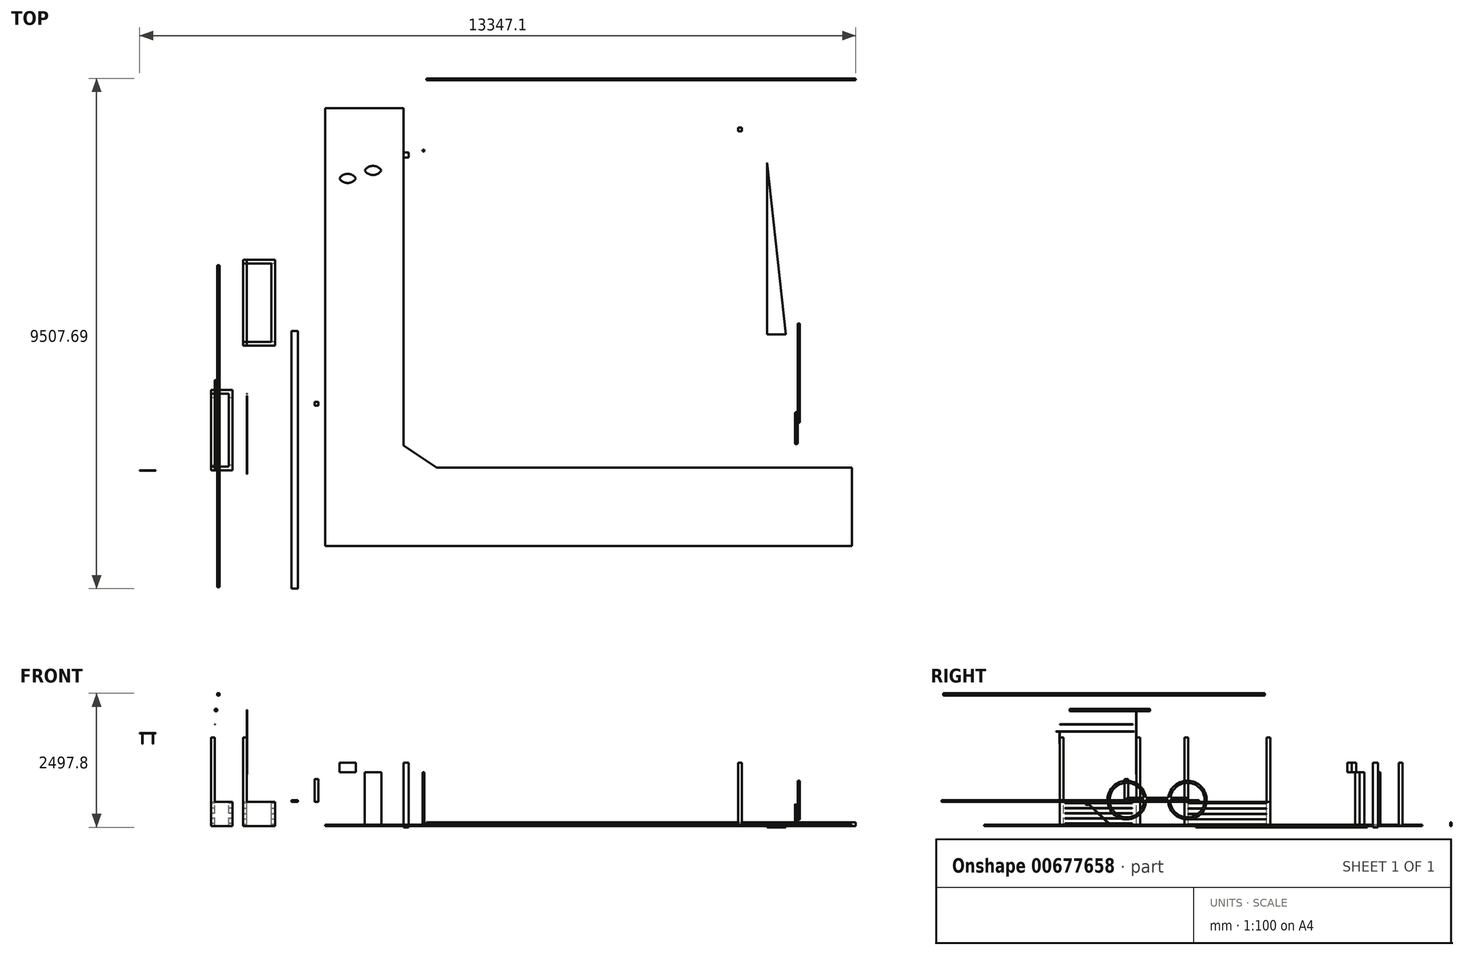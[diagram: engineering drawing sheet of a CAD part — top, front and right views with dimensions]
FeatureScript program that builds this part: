
annotation { "Feature Type Name" : "Feature", "Feature Type Description" : "" }
export const myFeature = defineFeature(function(context is Context, id is Id, definition is map)
    precondition{}
    {
        {
            var Q0;
            Q0=qCreatedBy(makeId("Top.planeOp"),FACE);
            var sketch = newSketch(context, id + "F0", { "sketchPlane" : qUnion([Q0])});
            skLineSegment(sketch, "E0.bottom", {"start": v(-6724.28, 5845.8) * mm, "end": v(50.72, 5845.8) * mm});
            skLineSegment(sketch, "E0.top", {"start": v(-6103.03, 165.8) * mm, "end": v(50.72, 165.8) * mm});
            skLineSegment(sketch, "E0.left", {"start": v(-6724.28, 5845.8) * mm, "end": v(-6724.28, 575.92) * mm});
            skLineSegment(sketch, "E0.right", {"start": v(50.72, 5845.8) * mm, "end": v(50.72, 165.8) * mm});
            skLineSegment(sketch, "E1.bottom", {"start": v(-449.28, 5845.8) * mm, "end": v(-379.28, 5845.8) * mm});
            skLineSegment(sketch, "E1.top", {"start": v(-449.28, 5915.8) * mm, "end": v(-379.28, 5915.8) * mm});
            skLineSegment(sketch, "E1.left", {"start": v(-449.28, 5845.8) * mm, "end": v(-449.28, 5915.8) * mm});
            skLineSegment(sketch, "E1.right", {"start": v(-379.28, 5845.8) * mm, "end": v(-379.28, 5915.8) * mm});
            skLineSegment(sketch, "E2.bottom", {"start": v(-2184.28, 5845.8) * mm, "end": v(-2254.28, 5845.8) * mm});
            skLineSegment(sketch, "E2.top", {"start": v(-2184.28, 5915.8) * mm, "end": v(-2254.28, 5915.8) * mm});
            skLineSegment(sketch, "E2.left", {"start": v(-2184.28, 5845.8) * mm, "end": v(-2184.28, 5915.8) * mm});
            skLineSegment(sketch, "E2.right", {"start": v(-2254.28, 5845.8) * mm, "end": v(-2254.28, 5915.8) * mm});
            skLineSegment(sketch, "E3.bottom", {"start": v(-4054.28, 5845.8) * mm, "end": v(-3984.28, 5845.8) * mm});
            skLineSegment(sketch, "E3.top", {"start": v(-4054.28, 5915.8) * mm, "end": v(-3984.28, 5915.8) * mm});
            skLineSegment(sketch, "E3.left", {"start": v(-4054.28, 5845.8) * mm, "end": v(-4054.28, 5915.8) * mm});
            skLineSegment(sketch, "E3.right", {"start": v(-3984.28, 5845.8) * mm, "end": v(-3984.28, 5915.8) * mm});
            skLineSegment(sketch, "E4.bottom", {"start": v(-5869.28, 5845.8) * mm, "end": v(-5799.28, 5845.8) * mm});
            skLineSegment(sketch, "E4.top", {"start": v(-5869.28, 5915.8) * mm, "end": v(-5799.28, 5915.8) * mm});
            skLineSegment(sketch, "E4.left", {"start": v(-5869.28, 5845.8) * mm, "end": v(-5869.28, 5915.8) * mm});
            skLineSegment(sketch, "E4.right", {"start": v(-5799.28, 5845.8) * mm, "end": v(-5799.28, 5915.8) * mm});
            skLineSegment(sketch, "E5.bottom", {"start": v(-6724.28, 5945.8) * mm, "end": v(-6629.28, 5945.8) * mm});
            skLineSegment(sketch, "E5.top", {"start": v(-6724.28, 6040.8) * mm, "end": v(-6629.28, 6040.8) * mm});
            skLineSegment(sketch, "E5.left", {"start": v(-6724.28, 5945.8) * mm, "end": v(-6724.28, 6040.8) * mm});
            skLineSegment(sketch, "E5.right", {"start": v(-6629.28, 5945.8) * mm, "end": v(-6629.28, 6040.8) * mm});
            skLineSegment(sketch, "E6", {"start": v(-6724.28, 575.92) * mm, "end": v(-6314.16, 165.8) * mm});
            skLineSegment(sketch, "E7", {"start": v(50.72, 5845.8) * mm, "end": v(50.72, 2645.8) * mm});
            skLineSegment(sketch, "E8", {"start": v(50.72, 2645.8) * mm, "end": v(400.72, 2645.8) * mm});
            skLineSegment(sketch, "E9", {"start": v(400.72, 2645.8) * mm, "end": v(50.72, 5845.8) * mm});
            skLineSegment(sketch, "E10", {"start": v(400.72, 2645.8) * mm, "end": v(671.97, 165.8) * mm});
            skLineSegment(sketch, "E11", {"start": v(50.72, 165.8) * mm, "end": v(671.97, 165.8) * mm});
            skLineSegment(sketch, "E12", {"start": v(-6724.28, 5845.8) * mm, "end": v(-6103.03, 165.8) * mm});
            skSolve(sketch);
        }
        {
            var Q0;
            Q0=makeQuery(id+"F0.imprint","IMPRINT",FACE,{"disambiguationData":[TD([[makeQuery(id+"F0.imprint","IMPRINT",EDGE,{"derivedFrom":sQuery(id+"F0.wireOp",EDGE,"E0.top")}),1.0]])]});
            var Q1;
            Q1=makeQuery(id+"F0.imprint","IMPRINT",FACE,{"disambiguationData":[TD([[makeQuery(id+"F0.imprint","IMPRINT",EDGE,{"derivedFrom":sQuery(id+"F0.wireOp",EDGE,"E1.bottom")}),1.0]])]});
            var Q2;
            Q2=makeQuery(id+"F0.imprint","IMPRINT",FACE,{"disambiguationData":[TD([[makeQuery(id+"F0.imprint","IMPRINT",EDGE,{"derivedFrom":sQuery(id+"F0.wireOp",EDGE,"E2.bottom")}),-1.0]])]});
            var Q3;
            Q3=makeQuery(id+"F0.imprint","IMPRINT",FACE,{"disambiguationData":[TD([[makeQuery(id+"F0.imprint","IMPRINT",EDGE,{"derivedFrom":sQuery(id+"F0.wireOp",EDGE,"E3.bottom")}),1.0]])]});
            var Q4;
            Q4=makeQuery(id+"F0.imprint","IMPRINT",FACE,{"disambiguationData":[TD([[makeQuery(id+"F0.imprint","IMPRINT",EDGE,{"derivedFrom":sQuery(id+"F0.wireOp",EDGE,"E4.bottom")}),1.0]])]});
            var Q5;
            Q5=makeQuery(id+"F0.imprint","IMPRINT",FACE,{"disambiguationData":[TD([[makeQuery(id+"F0.imprint","IMPRINT",EDGE,{"derivedFrom":sQuery(id+"F0.wireOp",EDGE,"E5.bottom")}),1.0]])]});
            var Q6;
            Q6=makeQuery(id+"F0.imprint","IMPRINT",FACE,{"disambiguationData":[TD([[makeQuery(id+"F0.imprint","IMPRINT",EDGE,{"derivedFrom":sQuery(id+"F0.wireOp",EDGE,"E0.right")}),1.0]])]});
            var Q7;
            Q7=makeQuery(id+"F0.imprint","IMPRINT",FACE,{"disambiguationData":[TD([[makeQuery(id+"F0.imprint","IMPRINT",EDGE,{"derivedFrom":sQuery(id+"F0.wireOp",EDGE,"E7")}),1.0]])]});
            extrude(context, id + "F1", {"entities" : qUnion([Q0, Q1, Q2, Q3, Q4, Q5, Q6, Q7]), "oppositeDirection" : true, "depth" : 25 * mm, "offsetDistance" : 25 * mm});
        }
        {
            var Q0;
            Q0=qCreatedBy(makeId("Top.planeOp"),FACE);
            var sketch = newSketch(context, id + "F2", { "sketchPlane" : qUnion([Q0])});
            skLineSegment(sketch, "E13.bottom", {"start": v(-484.06, 6502.45) * mm, "end": v(-414.06, 6502.45) * mm});
            skLineSegment(sketch, "E13.top", {"start": v(-484.06, 6432.45) * mm, "end": v(-414.06, 6432.45) * mm});
            skLineSegment(sketch, "E13.left", {"start": v(-484.06, 6502.45) * mm, "end": v(-484.06, 6432.45) * mm});
            skLineSegment(sketch, "E13.right", {"start": v(-414.06, 6502.45) * mm, "end": v(-414.06, 6432.45) * mm});
            skSolve(sketch);
        }
        {
            var Q0;
            Q0=makeQuery(id+"F2.imprint","IMPRINT",FACE,{"disambiguationData":[TD([[makeQuery(id+"F2.imprint","IMPRINT",EDGE,{"derivedFrom":sQuery(id+"F2.wireOp",EDGE,"E13.bottom")}),-1.0]])]});
            extrude(context, id + "F3", {"entities" : qUnion([Q0]), "depth" : 1180 * mm, "offsetDistance" : 25 * mm});
        }
        {
            var Q0;
            Q0=makeQuery(id+"F1.opExtrude","CAP_FACE",FACE,{"disambiguationData":[OSD([sQuery(id+"F0.wireOp",EDGE,"E5.bottom"),sQuery(id+"F0.wireOp",EDGE,"E5.top"),sQuery(id+"F0.wireOp",EDGE,"E5.left"),sQuery(id+"F0.wireOp",EDGE,"E5.right")])],"isStart":true});
            extrude(context, id + "F4", {"entities" : qUnion([Q0]), "operationType" : NewBodyOperationType.ADD, "depth" : 1180 * mm, "offsetDistance" : 25 * mm});
        }
        {
            var Q0;
            Q0=qCreatedBy(makeId("Top.planeOp"),FACE);
            var sketch = newSketch(context, id + "F5", { "sketchPlane" : qUnion([Q0])});
            skLineSegment(sketch, "E14.bottom", {"start": v(-6295.07, 7386.85) * mm, "end": v(1704.93, 7386.85) * mm});
            skLineSegment(sketch, "E14.top", {"start": v(-6295.07, 7416.85) * mm, "end": v(1704.93, 7416.85) * mm});
            skLineSegment(sketch, "E14.left", {"start": v(-6295.07, 7386.85) * mm, "end": v(-6295.07, 7416.85) * mm});
            skLineSegment(sketch, "E14.right", {"start": v(1704.93, 7386.85) * mm, "end": v(1704.93, 7416.85) * mm});
            skSolve(sketch);
        }
        {
            var Q0;
            Q0=makeQuery(id+"F5.imprint","IMPRINT",FACE,{"disambiguationData":[TD([[makeQuery(id+"F5.imprint","IMPRINT",EDGE,{"derivedFrom":sQuery(id+"F5.wireOp",EDGE,"E14.bottom")}),1.0]])]});
            extrude(context, id + "F6", {"entities" : qUnion([Q0]), "depth" : 70 * mm, "offsetDistance" : 25 * mm});
        }
        {
            var Q0;
            Q0=qCreatedBy(makeId("Top.planeOp"),FACE);
            var sketch = newSketch(context, id + "F7", { "sketchPlane" : qUnion([Q0])});
            skArc(sketch, "E15", {"start": v(-7135.8, 5703.5) * mm, "mid": v(-7290.8, 5788.5) * mm, "end": v(-7445.8, 5703.5) * mm});
            skLineSegment(sketch, "E16", {"start": v(-7477.04, 5788.5) * mm, "end": v(-7088.43, 5788.5) * mm});
            skLineSegment(sketch, "E17", {"start": v(-7445.8, 5703.5) * mm, "end": v(-7135.8, 5703.5) * mm});
            skArc(sketch, "E18.MirrorCS", {"start": v(-7135.8, 5703.5) * mm, "mid": v(-7290.8, 5618.5) * mm, "end": v(-7445.8, 5703.5) * mm});
            skSolve(sketch);
        }
        {
            var Q0;
            {var subQ1=sQuery(id+"F7.wireOp",EDGE,"E17");Q0=makeQuery(id+"F7.imprint","IMPRINT",FACE,{"disambiguationData":[TD([[makeQuery(id+"F7.imprint","IMPRINT",EDGE,{"derivedFrom":subQ1}),1.0]])]});}
            var Q1;
            Q1=makeQuery(id+"F7.imprint","IMPRINT",FACE,{"disambiguationData":[TD([[makeQuery(id+"F7.imprint","IMPRINT",EDGE,{"derivedFrom":sQuery(id+"F7.wireOp",EDGE,"E17")}),-1.0]])]});
            extrude(context, id + "F8", {"entities" : qUnion([Q0, Q1]), "depth" : 1000 * mm, "offsetDistance" : 25 * mm});
        }
        {
            var Q0;
            Q0=qCreatedBy(makeId("Top.planeOp"),FACE);
            var sketch = newSketch(context, id + "F9", { "sketchPlane" : qUnion([Q0])});
            skLineSegment(sketch, "E19.bottom", {"start": v(-6366.97, 6054.53) * mm, "end": v(-6331.97, 6054.53) * mm});
            skLineSegment(sketch, "E19.top", {"start": v(-6366.97, 6089.53) * mm, "end": v(-6331.97, 6089.53) * mm});
            skLineSegment(sketch, "E19.left", {"start": v(-6366.97, 6054.53) * mm, "end": v(-6366.97, 6089.53) * mm});
            skLineSegment(sketch, "E19.right", {"start": v(-6331.97, 6054.53) * mm, "end": v(-6331.97, 6089.53) * mm});
            skSolve(sketch);
        }
        {
            var Q0;
            Q0=makeQuery(id+"F9.imprint","IMPRINT",FACE,{"disambiguationData":[TD([[makeQuery(id+"F9.imprint","IMPRINT",EDGE,{"derivedFrom":sQuery(id+"F9.wireOp",EDGE,"E19.bottom")}),1.0]])]});
            extrude(context, id + "F10", {"entities" : qUnion([Q0]), "depth" : 1000 * mm, "offsetDistance" : 25 * mm});
        }
        {
            var Q0;
            Q0=qCreatedBy(makeId("Top.planeOp"),FACE);
            var sketch = newSketch(context, id + "F11", { "sketchPlane" : qUnion([Q0])});
            skLineSegment(sketch, "E20.bottom", {"start": v(-9714.32, 4035.91) * mm, "end": v(-9114.32, 4035.91) * mm});
            skLineSegment(sketch, "E20.top", {"start": v(-9714.32, 2435.91) * mm, "end": v(-9114.32, 2435.91) * mm});
            skLineSegment(sketch, "E20.left", {"start": v(-9714.32, 4035.91) * mm, "end": v(-9714.32, 2435.91) * mm});
            skLineSegment(sketch, "E20.right", {"start": v(-9114.32, 4035.91) * mm, "end": v(-9114.32, 2435.91) * mm});
            skSolve(sketch);
        }
        {
            var Q0;
            Q0=makeQuery(id+"F11.imprint","IMPRINT",FACE,{"disambiguationData":[TD([[makeQuery(id+"F11.imprint","IMPRINT",EDGE,{"derivedFrom":sQuery(id+"F11.wireOp",EDGE,"E20.bottom")}),-1.0]])]});
            extrude(context, id + "F12", {"entities" : qUnion([Q0]), "depth" : 450 * mm, "offsetDistance" : 25 * mm});
        }
        {
            var Q0;
            Q0=makeQuery(id+"F12.opExtrude","SWEPT_FACE",FACE,{"disambiguationData":[OSD([sQuery(id+"F11.wireOp",EDGE,"E20.left")])]});
            var sketch = newSketch(context, id + "F13", { "sketchPlane" : qUnion([Q0])});
            skLineSegment(sketch, "E21.bottom", {"start": v(-3965.91, 428) * mm, "end": v(-2505.91, 428) * mm});
            skLineSegment(sketch, "E21.top", {"start": v(-3965.91, 423) * mm, "end": v(-2505.91, 423) * mm});
            skLineSegment(sketch, "E21.left", {"start": v(-3965.91, 428) * mm, "end": v(-3965.91, 423) * mm});
            skLineSegment(sketch, "E21.right", {"start": v(-2505.91, 428) * mm, "end": v(-2505.91, 423) * mm});
            skLineSegment(sketch, "E22.0.1.0", {"start": v(-3965.91, 328) * mm, "end": v(-2505.91, 328) * mm});
            skLineSegment(sketch, "E22.0.1.1", {"start": v(-3965.91, 323) * mm, "end": v(-2505.91, 323) * mm});
            skLineSegment(sketch, "E22.0.1.2", {"start": v(-3965.91, 328) * mm, "end": v(-3965.91, 323) * mm});
            skLineSegment(sketch, "E22.0.1.3", {"start": v(-2505.91, 328) * mm, "end": v(-2505.91, 323) * mm});
            skLineSegment(sketch, "E22.0.2.0", {"start": v(-3965.91, 228) * mm, "end": v(-2505.91, 228) * mm});
            skLineSegment(sketch, "E22.0.2.1", {"start": v(-3965.91, 223) * mm, "end": v(-2505.91, 223) * mm});
            skLineSegment(sketch, "E22.0.2.2", {"start": v(-3965.91, 228) * mm, "end": v(-3965.91, 223) * mm});
            skLineSegment(sketch, "E22.0.2.3", {"start": v(-2505.91, 228) * mm, "end": v(-2505.91, 223) * mm});
            skLineSegment(sketch, "E22.0.3.0", {"start": v(-3965.91, 128) * mm, "end": v(-2505.91, 128) * mm});
            skLineSegment(sketch, "E22.0.3.1", {"start": v(-3965.91, 123) * mm, "end": v(-2505.91, 123) * mm});
            skLineSegment(sketch, "E22.0.3.2", {"start": v(-3965.91, 128) * mm, "end": v(-3965.91, 123) * mm});
            skLineSegment(sketch, "E22.0.3.3", {"start": v(-2505.91, 128) * mm, "end": v(-2505.91, 123) * mm});
            skLineSegment(sketch, "E22.0.4.0", {"start": v(-3965.91, 28) * mm, "end": v(-2505.91, 28) * mm});
            skLineSegment(sketch, "E22.0.4.1", {"start": v(-3965.91, 23) * mm, "end": v(-2505.91, 23) * mm});
            skLineSegment(sketch, "E22.0.4.2", {"start": v(-3965.91, 28) * mm, "end": v(-3965.91, 23) * mm});
            skLineSegment(sketch, "E22.0.4.3", {"start": v(-2505.91, 28) * mm, "end": v(-2505.91, 23) * mm});
            skLineSegment(sketch, "E22.0.5.0", {"start": v(-3965.91, -72) * mm, "end": v(-2505.91, -72) * mm});
            skLineSegment(sketch, "E22.0.5.1", {"start": v(-3965.91, -77) * mm, "end": v(-2505.91, -77) * mm});
            skLineSegment(sketch, "E22.0.5.2", {"start": v(-3965.91, -72) * mm, "end": v(-3965.91, -77) * mm});
            skLineSegment(sketch, "E22.0.5.3", {"start": v(-2505.91, -72) * mm, "end": v(-2505.91, -77) * mm});
            skLineSegment(sketch, "E22.0.6.0", {"start": v(-3965.91, -172) * mm, "end": v(-2505.91, -172) * mm});
            skLineSegment(sketch, "E22.0.6.1", {"start": v(-3965.91, -177) * mm, "end": v(-2505.91, -177) * mm});
            skLineSegment(sketch, "E22.0.6.2", {"start": v(-3965.91, -172) * mm, "end": v(-3965.91, -177) * mm});
            skLineSegment(sketch, "E22.0.6.3", {"start": v(-2505.91, -172) * mm, "end": v(-2505.91, -177) * mm});
            skLineSegment(sketch, "E22.0.7.0", {"start": v(-3965.91, -272) * mm, "end": v(-2505.91, -272) * mm});
            skLineSegment(sketch, "E22.0.7.1", {"start": v(-3965.91, -277) * mm, "end": v(-2505.91, -277) * mm});
            skLineSegment(sketch, "E22.0.7.2", {"start": v(-3965.91, -272) * mm, "end": v(-3965.91, -277) * mm});
            skLineSegment(sketch, "E22.0.7.3", {"start": v(-2505.91, -272) * mm, "end": v(-2505.91, -277) * mm});
            skLineSegment(sketch, "E22.0.8.0", {"start": v(-3965.91, -372) * mm, "end": v(-2505.91, -372) * mm});
            skLineSegment(sketch, "E22.0.8.1", {"start": v(-3965.91, -377) * mm, "end": v(-2505.91, -377) * mm});
            skLineSegment(sketch, "E22.0.8.2", {"start": v(-3965.91, -372) * mm, "end": v(-3965.91, -377) * mm});
            skLineSegment(sketch, "E22.0.8.3", {"start": v(-2505.91, -372) * mm, "end": v(-2505.91, -377) * mm});
            skLineSegment(sketch, "E22.direction1", {"start": v(-3965.91, 423) * mm, "end": v(-3652.23, 423) * mm, "construction": true});
            skLineSegment(sketch, "E22.direction2", {"start": v(-3965.91, 423) * mm, "end": v(-3965.91, 323) * mm, "construction": true});
            skSolve(sketch);
        }
        {
            var Q0;
            Q0=makeQuery(id+"F13.imprint","IMPRINT",FACE,{"disambiguationData":[TD([[makeQuery(id+"F13.imprint","IMPRINT",EDGE,{"derivedFrom":sQuery(id+"F13.wireOp",EDGE,"E21.bottom")}),-1.0]])]});
            var Q1;
            Q1=makeQuery(id+"F13.imprint","IMPRINT",FACE,{"disambiguationData":[TD([[makeQuery(id+"F13.imprint","IMPRINT",EDGE,{"derivedFrom":sQuery(id+"F13.wireOp",EDGE,"E22.0.1.0")}),-1.0]])]});
            var Q2;
            Q2=makeQuery(id+"F13.imprint","IMPRINT",FACE,{"disambiguationData":[TD([[makeQuery(id+"F13.imprint","IMPRINT",EDGE,{"derivedFrom":sQuery(id+"F13.wireOp",EDGE,"E22.0.2.0")}),-1.0]])]});
            var Q3;
            Q3=makeQuery(id+"F13.imprint","IMPRINT",FACE,{"disambiguationData":[TD([[makeQuery(id+"F13.imprint","IMPRINT",EDGE,{"derivedFrom":sQuery(id+"F13.wireOp",EDGE,"E22.0.3.0")}),-1.0]])]});
            var Q4;
            Q4=makeQuery(id+"F13.imprint","IMPRINT",FACE,{"disambiguationData":[TD([[makeQuery(id+"F13.imprint","IMPRINT",EDGE,{"derivedFrom":sQuery(id+"F13.wireOp",EDGE,"E22.0.4.0")}),-1.0]])]});
            var Q5;
            Q5=makeQuery(id+"F13.imprint","IMPRINT",FACE,{"disambiguationData":[TD([[makeQuery(id+"F13.imprint","IMPRINT",EDGE,{"derivedFrom":sQuery(id+"F13.wireOp",EDGE,"E22.0.5.0")}),-1.0]])]});
            var Q6;
            Q6=makeQuery(id+"F13.imprint","IMPRINT",FACE,{"disambiguationData":[TD([[makeQuery(id+"F13.imprint","IMPRINT",EDGE,{"derivedFrom":sQuery(id+"F13.wireOp",EDGE,"E22.0.6.0")}),-1.0]])]});
            var Q7;
            Q7=makeQuery(id+"F13.imprint","IMPRINT",FACE,{"disambiguationData":[TD([[makeQuery(id+"F13.imprint","IMPRINT",EDGE,{"derivedFrom":sQuery(id+"F13.wireOp",EDGE,"E22.0.7.0")}),-1.0]])]});
            var Q8;
            Q8=makeQuery(id+"F13.imprint","IMPRINT",FACE,{"disambiguationData":[TD([[makeQuery(id+"F13.imprint","IMPRINT",EDGE,{"derivedFrom":sQuery(id+"F13.wireOp",EDGE,"E22.0.8.0")}),-1.0]])]});
            extrude(context, id + "F14", {"entities" : qUnion([Q0, Q1, Q2, Q3, Q4, Q5, Q6, Q7, Q8]), "operationType" : NewBodyOperationType.REMOVE, "oppositeDirection" : true, "depth" : 700 * mm, "offsetDistance" : 25 * mm});
        }
        {
            var Q0;
            Q0=makeQuery(id+"F12.opExtrude","CAP_FACE",FACE,{"disambiguationData":[OSD([sQuery(id+"F11.wireOp",EDGE,"E20.bottom"),sQuery(id+"F11.wireOp",EDGE,"E20.top"),sQuery(id+"F11.wireOp",EDGE,"E20.left"),sQuery(id+"F11.wireOp",EDGE,"E20.right")])],"isStart":false});
            var sketch = newSketch(context, id + "F15", { "sketchPlane" : qUnion([Q0])});
            skLineSegment(sketch, "E23.bottom", {"start": v(-9714.32, 4035.91) * mm, "end": v(-9644.32, 4035.91) * mm});
            skLineSegment(sketch, "E23.top", {"start": v(-9714.32, 3965.91) * mm, "end": v(-9644.32, 3965.91) * mm});
            skLineSegment(sketch, "E23.left", {"start": v(-9714.32, 4035.91) * mm, "end": v(-9714.32, 3965.91) * mm});
            skLineSegment(sketch, "E23.right", {"start": v(-9644.32, 4035.91) * mm, "end": v(-9644.32, 3965.91) * mm});
            skLineSegment(sketch, "E24.bottom", {"start": v(-9714.32, 2435.91) * mm, "end": v(-9644.32, 2435.91) * mm});
            skLineSegment(sketch, "E24.top", {"start": v(-9714.32, 2505.91) * mm, "end": v(-9644.32, 2505.91) * mm});
            skLineSegment(sketch, "E24.left", {"start": v(-9714.32, 2435.91) * mm, "end": v(-9714.32, 2505.91) * mm});
            skLineSegment(sketch, "E24.right", {"start": v(-9644.32, 2435.91) * mm, "end": v(-9644.32, 2505.91) * mm});
            skSolve(sketch);
        }
        {
            var Q0;
            Q0=makeQuery(id+"F15.imprint","IMPRINT",FACE,{"disambiguationData":[TD([[makeQuery(id+"F15.imprint","IMPRINT",EDGE,{"derivedFrom":sQuery(id+"F15.wireOp",EDGE,"E23.bottom")}),-1.0]])]});
            var Q1;
            Q1=makeQuery(id+"F15.imprint","IMPRINT",FACE,{"disambiguationData":[TD([[makeQuery(id+"F15.imprint","IMPRINT",EDGE,{"derivedFrom":sQuery(id+"F15.wireOp",EDGE,"E24.bottom")}),1.0]])]});
            extrude(context, id + "F16", {"entities" : qUnion([Q0, Q1]), "operationType" : NewBodyOperationType.ADD, "depth" : 1200 * mm, "offsetDistance" : 25 * mm});
        }
        {
            var Q0;
            Q0=makeQuery(id+"F16.opExtrude","SWEPT_FACE",FACE,{"disambiguationData":[OSD([sQuery(id+"F15.wireOp",EDGE,"E24.right")])]});
            var sketch = newSketch(context, id + "F17", { "sketchPlane" : qUnion([Q0])});
            skLineSegment(sketch, "E25.bottom", {"start": v(43.28, 1763.08) * mm, "end": v(1503.28, 1763.08) * mm});
            skLineSegment(sketch, "E25.top", {"start": v(43.28, 1758.08) * mm, "end": v(1503.28, 1758.08) * mm});
            skLineSegment(sketch, "E25.left", {"start": v(43.28, 1763.08) * mm, "end": v(43.28, 1758.08) * mm});
            skLineSegment(sketch, "E25.right", {"start": v(1503.28, 1763.08) * mm, "end": v(1503.28, 1758.08) * mm});
            skLineSegment(sketch, "E26.bottom", {"start": v(1534.4, 2162.34) * mm, "end": v(1539.4, 2162.34) * mm});
            skLineSegment(sketch, "E26.top", {"start": v(1534.4, 962.34) * mm, "end": v(1539.4, 962.34) * mm});
            skLineSegment(sketch, "E26.left", {"start": v(1534.4, 2162.34) * mm, "end": v(1534.4, 962.34) * mm});
            skLineSegment(sketch, "E26.right", {"start": v(1539.4, 2162.34) * mm, "end": v(1539.4, 962.34) * mm});
            skSolve(sketch);
        }
        {
            var Q0;
            Q0=makeQuery(id+"F17.imprint","IMPRINT",FACE,{"disambiguationData":[TD([[makeQuery(id+"F17.imprint","IMPRINT",EDGE,{"derivedFrom":sQuery(id+"F17.wireOp",EDGE,"E25.bottom")}),-1.0]])]});
            var Q1;
            Q1=makeQuery(id+"F17.imprint","IMPRINT",FACE,{"disambiguationData":[TD([[makeQuery(id+"F17.imprint","IMPRINT",EDGE,{"derivedFrom":sQuery(id+"F17.wireOp",EDGE,"E26.bottom")}),-1.0]])]});
            extrude(context, id + "F18", {"entities" : qUnion([Q0, Q1]), "depth" : 5 * mm, "offsetDistance" : 25 * mm});
        }
        {
            var Q0;
            Q0=makeQuery(id+"F12.opExtrude","CAP_FACE",FACE,{"disambiguationData":[OSD([sQuery(id+"F11.wireOp",EDGE,"E20.bottom"),sQuery(id+"F11.wireOp",EDGE,"E20.top"),sQuery(id+"F11.wireOp",EDGE,"E20.left"),sQuery(id+"F11.wireOp",EDGE,"E20.right")])],"isStart":false});
            var sketch = newSketch(context, id + "F19", { "sketchPlane" : qUnion([Q0])});
            skLineSegment(sketch, "E27.bottom", {"start": v(-9644.32, 3965.91) * mm, "end": v(-9184.32, 3965.91) * mm});
            skLineSegment(sketch, "E27.top", {"start": v(-9644.32, 2505.91) * mm, "end": v(-9184.32, 2505.91) * mm});
            skLineSegment(sketch, "E27.left", {"start": v(-9644.32, 3965.91) * mm, "end": v(-9644.32, 2505.91) * mm});
            skLineSegment(sketch, "E27.right", {"start": v(-9184.32, 3965.91) * mm, "end": v(-9184.32, 2505.91) * mm});
            skSolve(sketch);
        }
        {
            var Q0;
            Q0=makeQuery(id+"F19.imprint","IMPRINT",FACE,{"disambiguationData":[TD([[makeQuery(id+"F19.imprint","IMPRINT",EDGE,{"derivedFrom":sQuery(id+"F19.wireOp",EDGE,"E27.bottom")}),-1.0]])]});
            extrude(context, id + "F20", {"entities" : qUnion([Q0]), "operationType" : NewBodyOperationType.REMOVE, "oppositeDirection" : true, "depth" : 680 * mm, "offsetDistance" : 25 * mm});
        }
        {
            var Q0;
            Q0=makeQuery(id+"F8.opExtrude","CAP_FACE",FACE,{"disambiguationData":[OSD([sQuery(id+"F7.wireOp",EDGE,"E15"),sQuery(id+"F7.wireOp",EDGE,"E18.MirrorCS")])],"isStart":false});
            var sketch = newSketch(context, id + "F21", { "sketchPlane" : qUnion([Q0])});
            skLineSegment(sketch, "E28", {"start": v(-7918.47, 5554) * mm, "end": v(-7608.47, 5554) * mm});
            skLineSegment(sketch, "E29", {"start": v(-7608.47, 5554) * mm, "end": v(-7608.47, 5639) * mm});
            skLineSegment(sketch, "E30", {"start": v(-7608.47, 5639) * mm, "end": v(-8001.82, 5639) * mm});
            skArc(sketch, "E31", {"start": v(-7608.47, 5554) * mm, "mid": v(-7763.47, 5639) * mm, "end": v(-7918.47, 5554) * mm});
            skArc(sketch, "E32.MirrorCS", {"start": v(-7608.47, 5554) * mm, "mid": v(-7763.47, 5469) * mm, "end": v(-7918.47, 5554) * mm});
            skSolve(sketch);
        }
        {
            var Q0;
            {var subQ0=sQuery(id+"F21.wireOp",EDGE,"E28");Q0=makeQuery(id+"F21.imprint","IMPRINT",FACE,{"disambiguationData":[TD([[makeQuery(id+"F21.imprint","IMPRINT",EDGE,{"derivedFrom":subQ0}),1.0]])]});}
            var Q1;
            Q1=makeQuery(id+"F21.imprint","IMPRINT",FACE,{"disambiguationData":[TD([[makeQuery(id+"F21.imprint","IMPRINT",EDGE,{"derivedFrom":sQuery(id+"F21.wireOp",EDGE,"E28")}),-1.0]])]});
            extrude(context, id + "F22", {"entities" : qUnion([Q0, Q1]), "depth" : 180 * mm, "offsetDistance" : 25 * mm});
        }
        {
            var Q0;
            Q0=makeQuery(id+"F1.opExtrude","CAP_FACE",FACE,{"disambiguationData":[OSD([sQuery(id+"F0.wireOp",EDGE,"E0.bottom"),sQuery(id+"F0.wireOp",EDGE,"E0.top"),sQuery(id+"F0.wireOp",EDGE,"E0.left"),sQuery(id+"F0.wireOp",EDGE,"E0.right"),sQuery(id+"F0.wireOp",EDGE,"E1.top"),sQuery(id+"F0.wireOp",EDGE,"E1.left"),sQuery(id+"F0.wireOp",EDGE,"E1.right"),sQuery(id+"F0.wireOp",EDGE,"E2.top"),sQuery(id+"F0.wireOp",EDGE,"E2.left"),sQuery(id+"F0.wireOp",EDGE,"E2.right"),sQuery(id+"F0.wireOp",EDGE,"E3.top"),sQuery(id+"F0.wireOp",EDGE,"E3.left"),sQuery(id+"F0.wireOp",EDGE,"E3.right"),sQuery(id+"F0.wireOp",EDGE,"E4.top"),sQuery(id+"F0.wireOp",EDGE,"E4.left"),sQuery(id+"F0.wireOp",EDGE,"E4.right"),sQuery(id+"F0.wireOp",EDGE,"E6")])],"isStart":true});
            var sketch = newSketch(context, id + "F23", { "sketchPlane" : qUnion([Q0])});
            skLineSegment(sketch, "E33", {"start": v(-6724.28, 5845.8) * mm, "end": v(-6724.28, 575.92) * mm});
            skLineSegment(sketch, "E34", {"start": v(-6724.28, 575.92) * mm, "end": v(-6103.03, 165.8) * mm});
            skLineSegment(sketch, "E35", {"start": v(-6103.03, 165.8) * mm, "end": v(1636.76, 165.8) * mm});
            skLineSegment(sketch, "E36", {"start": v(1636.76, 165.8) * mm, "end": v(1636.76, -1294.2) * mm});
            skLineSegment(sketch, "E37", {"start": v(1636.76, -1294.2) * mm, "end": v(-8184.28, -1294.2) * mm});
            skLineSegment(sketch, "E38", {"start": v(-8184.28, -1294.2) * mm, "end": v(-8184.28, 6866.58) * mm});
            skLineSegment(sketch, "E39", {"start": v(-8184.28, 6866.58) * mm, "end": v(-6724.28, 6866.58) * mm});
            skLineSegment(sketch, "E40", {"start": v(-6724.28, 6866.58) * mm, "end": v(-6724.28, 5845.8) * mm});
            skSolve(sketch);
        }
        {
            var Q0;
            Q0=makeQuery(id+"F23.imprint","IMPRINT",FACE,{"disambiguationData":[TD([[makeQuery(id+"F23.imprint","IMPRINT",EDGE,{"derivedFrom":sQuery(id+"F23.wireOp",EDGE,"E33")}),-1.0]])]});
            extrude(context, id + "F24", {"entities" : qUnion([Q0]), "depth" : 25 * mm, "offsetDistance" : 25 * mm});
        }
        {
            var Q0;
            Q0=makeQuery(id+"F1.opExtrude","CAP_FACE",FACE,{"disambiguationData":[OSD([sQuery(id+"F0.wireOp",EDGE,"E0.bottom"),sQuery(id+"F0.wireOp",EDGE,"E0.top"),sQuery(id+"F0.wireOp",EDGE,"E0.left"),sQuery(id+"F0.wireOp",EDGE,"E0.right"),sQuery(id+"F0.wireOp",EDGE,"E1.top"),sQuery(id+"F0.wireOp",EDGE,"E1.left"),sQuery(id+"F0.wireOp",EDGE,"E1.right"),sQuery(id+"F0.wireOp",EDGE,"E2.top"),sQuery(id+"F0.wireOp",EDGE,"E2.left"),sQuery(id+"F0.wireOp",EDGE,"E2.right"),sQuery(id+"F0.wireOp",EDGE,"E3.top"),sQuery(id+"F0.wireOp",EDGE,"E3.left"),sQuery(id+"F0.wireOp",EDGE,"E3.right"),sQuery(id+"F0.wireOp",EDGE,"E4.top"),sQuery(id+"F0.wireOp",EDGE,"E4.left"),sQuery(id+"F0.wireOp",EDGE,"E4.right"),sQuery(id+"F0.wireOp",EDGE,"E6")])],"isStart":true});
            var sketch = newSketch(context, id + "F25", { "sketchPlane" : qUnion([Q0])});
            skLineSegment(sketch, "E41.bottom", {"start": v(599.92, 1199.52) * mm, "end": v(597.92, 1199.52) * mm});
            skLineSegment(sketch, "E41.top", {"start": v(599.92, 599.52) * mm, "end": v(597.92, 599.52) * mm});
            skLineSegment(sketch, "E41.left", {"start": v(623.92, 1175.52) * mm, "end": v(623.92, 623.52) * mm});
            skLineSegment(sketch, "E41.right", {"start": v(573.92, 1175.52) * mm, "end": v(573.92, 623.52) * mm});
            skPoint(sketch, "E42.visualSharp", {"position": v(573.92, 1199.52) * mm});
            skArc(sketch, "E42.filletArc", {"start": v(597.92, 1199.52) * mm, "mid": v(580.95, 1192.5) * mm, "end": v(573.92, 1175.52) * mm});
            skPoint(sketch, "E43.visualSharp", {"position": v(623.92, 1199.52) * mm});
            skArc(sketch, "E43.filletArc", {"start": v(623.92, 1175.52) * mm, "mid": v(616.9, 1192.5) * mm, "end": v(599.92, 1199.52) * mm});
            skPoint(sketch, "E44.visualSharp", {"position": v(623.92, 599.52) * mm});
            skArc(sketch, "E44.filletArc", {"start": v(599.92, 599.52) * mm, "mid": v(616.9, 606.55) * mm, "end": v(623.92, 623.52) * mm});
            skPoint(sketch, "E45.visualSharp", {"position": v(573.92, 599.52) * mm});
            skArc(sketch, "E45.filletArc", {"start": v(573.92, 623.52) * mm, "mid": v(580.95, 606.55) * mm, "end": v(597.92, 599.52) * mm});
            skArc(sketch, "E46.0", {"start": v(597.92, 1191.52) * mm, "mid": v(586.6, 1186.84) * mm, "end": v(581.92, 1175.52) * mm});
            skLineSegment(sketch, "E46.1", {"start": v(599.92, 1191.52) * mm, "end": v(597.92, 1191.52) * mm});
            skLineSegment(sketch, "E46.2", {"start": v(581.92, 1175.52) * mm, "end": v(581.92, 623.52) * mm});
            skArc(sketch, "E46.3", {"start": v(615.92, 1175.52) * mm, "mid": v(611.23, 1186.84) * mm, "end": v(599.92, 1191.52) * mm});
            skArc(sketch, "E46.4", {"start": v(581.92, 623.52) * mm, "mid": v(586.6, 612.21) * mm, "end": v(597.92, 607.52) * mm});
            skLineSegment(sketch, "E46.5", {"start": v(599.92, 607.52) * mm, "end": v(597.92, 607.52) * mm});
            skArc(sketch, "E46.6", {"start": v(599.92, 607.52) * mm, "mid": v(611.23, 612.21) * mm, "end": v(615.92, 623.52) * mm});
            skLineSegment(sketch, "E46.7", {"start": v(615.92, 1175.52) * mm, "end": v(615.92, 623.52) * mm});
            skSolve(sketch);
        }
        {
            var Q0;
            Q0=makeQuery(id+"F25.imprint","IMPRINT",FACE,{"disambiguationData":[TD([[makeQuery(id+"F25.imprint","IMPRINT",EDGE,{"derivedFrom":sQuery(id+"F25.wireOp",EDGE,"E41.bottom")}),1.0]])]});
            extrude(context, id + "F26", {"entities" : qUnion([Q0]), "depth" : 400 * mm, "offsetDistance" : 25 * mm});
        }
        {
            var Q0;
            Q0=makeQuery(id+"F26.opExtrude","SWEPT_FACE",FACE,{"disambiguationData":[OSD([sQuery(id+"F25.wireOp",EDGE,"E41.left")])]});
            var sketch = newSketch(context, id + "F27", { "sketchPlane" : qUnion([Q0])});
            skLineSegment(sketch, "E47", {"start": v(400.9, 392) * mm, "end": v(664.2, 392) * mm});
            skLineSegment(sketch, "E48", {"start": v(664.2, 392) * mm, "end": v(1065.78, 0) * mm});
            skLineSegment(sketch, "E49", {"start": v(1065.78, 0) * mm, "end": v(1075.44, 0) * mm});
            skLineSegment(sketch, "E50", {"start": v(1075.44, 0) * mm, "end": v(1075.44, -239.66) * mm});
            skLineSegment(sketch, "E51", {"start": v(1075.44, -239.66) * mm, "end": v(417.05, -229.8) * mm});
            skLineSegment(sketch, "E52", {"start": v(417.05, -229.8) * mm, "end": v(400.9, 392) * mm});
            skLineSegment(sketch, "E53", {"start": v(667.45, 400) * mm, "end": v(1069.04, 8) * mm});
            skLineSegment(sketch, "E54", {"start": v(1069.04, 8) * mm, "end": v(1266.16, 8) * mm});
            skLineSegment(sketch, "E55", {"start": v(1266.16, 8) * mm, "end": v(1215.61, 445.54) * mm});
            skLineSegment(sketch, "E56", {"start": v(1215.61, 445.54) * mm, "end": v(670.1, 465.26) * mm});
            skLineSegment(sketch, "E57", {"start": v(670.1, 465.26) * mm, "end": v(667.45, 400) * mm});
            skSolve(sketch);
        }
        {
            var Q0;
            {var subQ0=sQuery(id+"F27.wireOp",EDGE,"E49");Q0=makeQuery(id+"F27.imprint","IMPRINT",FACE,{"disambiguationData":[TD([[makeQuery(id+"F27.imprint","IMPRINT",EDGE,{"derivedFrom":subQ0}),1.0]])]});}
            var Q1;
            {var subQ0=sQuery(id+"F27.wireOp",EDGE,"E48");Q1=makeQuery(id+"F27.imprint","IMPRINT",FACE,{"disambiguationData":[TD([[makeQuery(id+"F27.imprint","IMPRINT",EDGE,{"derivedFrom":subQ0}),-1.0]])]});}
            var Q2;
            {var subQ1=sQuery(id+"F27.wireOp",EDGE,"E55");Q2=makeQuery(id+"F27.imprint","IMPRINT",FACE,{"disambiguationData":[TD([[makeQuery(id+"F27.imprint","IMPRINT",EDGE,{"derivedFrom":subQ1}),1.0]])]});}
            var Q3;
            {var subQ0=sQuery(id+"F27.wireOp",EDGE,"E53");Q3=makeQuery(id+"F27.imprint","IMPRINT",FACE,{"disambiguationData":[TD([[makeQuery(id+"F27.imprint","IMPRINT",EDGE,{"derivedFrom":subQ0}),1.0]])]});}
            extrude(context, id + "F28", {"entities" : qUnion([Q0, Q1, Q2, Q3]), "operationType" : NewBodyOperationType.REMOVE, "oppositeDirection" : true, "depth" : 55 * mm, "offsetDistance" : 25 * mm});
        }
        {
            var Q0;
            Q0=makeQuery(id+"F26.opExtrude","SWEPT_FACE",FACE,{"disambiguationData":[OSD([sQuery(id+"F25.wireOp",EDGE,"E41.left")])]});
            var sketch = newSketch(context, id + "F29", { "sketchPlane" : qUnion([Q0])});
            skArc(sketch, "E58", {"start": v(1718.71, 526.1) * mm, "mid": v(1002.14, 459.54) * mm, "end": v(1721.45, 481.75) * mm});
            skArc(sketch, "E59", {"start": v(1678.37, 526.1) * mm, "mid": v(1042.23, 459.53) * mm, "end": v(1681.45, 481.75) * mm});
            skLineSegment(sketch, "E60", {"start": v(1361.45, 481.75) * mm, "end": v(1681.45, 481.75) * mm});
            skLineSegment(sketch, "E61", {"start": v(2491.45, 481.75) * mm, "end": v(2491.45, 526.1) * mm});
            skLineSegment(sketch, "E62", {"start": v(2491.45, 526.1) * mm, "end": v(2174.54, 526.1) * mm});
            skLineSegment(sketch, "E63", {"start": v(1361.45, 526.1) * mm, "end": v(1361.45, 481.75) * mm});
            skArc(sketch, "E64", {"start": v(2131.45, 481.75) * mm, "mid": v(2850.77, 459.54) * mm, "end": v(2134.2, 526.1) * mm});
            skArc(sketch, "E65", {"start": v(2171.45, 481.75) * mm, "mid": v(2810.68, 459.53) * mm, "end": v(2174.54, 526.1) * mm});
            skLineSegment(sketch, "E66.trimOffspring", {"start": v(1678.37, 526.1) * mm, "end": v(1361.45, 526.1) * mm});
            skLineSegment(sketch, "E67.trimOffspring", {"start": v(1721.45, 481.75) * mm, "end": v(2131.45, 481.75) * mm});
            skLineSegment(sketch, "E68.trimOffspring", {"start": v(2134.2, 526.1) * mm, "end": v(1718.71, 526.1) * mm});
            skLineSegment(sketch, "E69.trimOffspring", {"start": v(2171.45, 481.75) * mm, "end": v(2491.45, 481.75) * mm});
            skSolve(sketch);
        }
        {
            var Q0;
            Q0=makeQuery(id+"F29.imprint","IMPRINT",FACE,{"disambiguationData":[TD([[makeQuery(id+"F29.imprint","IMPRINT",EDGE,{"derivedFrom":sQuery(id+"F29.wireOp",EDGE,"E58")}),1.0]])]});
            extrude(context, id + "F30", {"entities" : qUnion([Q0]), "depth" : 40 * mm, "offsetDistance" : 25 * mm});
        }
        {
            var Q0;
            Q0=makeQuery(id+"F1.opExtrude","CAP_FACE",FACE,{"disambiguationData":[OSD([sQuery(id+"F0.wireOp",EDGE,"E0.bottom"),sQuery(id+"F0.wireOp",EDGE,"E0.top"),sQuery(id+"F0.wireOp",EDGE,"E0.left"),sQuery(id+"F0.wireOp",EDGE,"E0.right"),sQuery(id+"F0.wireOp",EDGE,"E1.top"),sQuery(id+"F0.wireOp",EDGE,"E1.left"),sQuery(id+"F0.wireOp",EDGE,"E1.right"),sQuery(id+"F0.wireOp",EDGE,"E2.top"),sQuery(id+"F0.wireOp",EDGE,"E2.left"),sQuery(id+"F0.wireOp",EDGE,"E2.right"),sQuery(id+"F0.wireOp",EDGE,"E3.top"),sQuery(id+"F0.wireOp",EDGE,"E3.left"),sQuery(id+"F0.wireOp",EDGE,"E3.right"),sQuery(id+"F0.wireOp",EDGE,"E4.top"),sQuery(id+"F0.wireOp",EDGE,"E4.left"),sQuery(id+"F0.wireOp",EDGE,"E4.right"),sQuery(id+"F0.wireOp",EDGE,"E6")])],"isStart":true});
            var sketch = newSketch(context, id + "F31", { "sketchPlane" : qUnion([Q0])});
            skLineSegment(sketch, "E70.bottom", {"start": v(-9910.47, 1611.68) * mm, "end": v(-10310.47, 1611.68) * mm});
            skLineSegment(sketch, "E70.top", {"start": v(-9910.47, 111.68) * mm, "end": v(-10310.47, 111.68) * mm});
            skLineSegment(sketch, "E70.left", {"start": v(-9910.47, 1611.68) * mm, "end": v(-9910.47, 111.68) * mm});
            skLineSegment(sketch, "E70.right", {"start": v(-10310.47, 1611.68) * mm, "end": v(-10310.47, 111.68) * mm});
            skSolve(sketch);
        }
        {
            var Q0;
            Q0=makeQuery(id+"F31.imprint","IMPRINT",FACE,{"disambiguationData":[TD([[makeQuery(id+"F31.imprint","IMPRINT",EDGE,{"derivedFrom":sQuery(id+"F31.wireOp",EDGE,"E70.bottom")}),1.0]])]});
            extrude(context, id + "F32", {"entities" : qUnion([Q0]), "depth" : 450 * mm, "offsetDistance" : 25 * mm});
        }
        {
            var Q0;
            Q0=makeQuery(id+"F32.opExtrude","SWEPT_FACE",FACE,{"disambiguationData":[OSD([sQuery(id+"F31.wireOp",EDGE,"E70.right")])]});
            var sketch = newSketch(context, id + "F33", { "sketchPlane" : qUnion([Q0])});
            skLineSegment(sketch, "E71.bottom", {"start": v(-1516.68, 430) * mm, "end": v(-206.68, 430) * mm});
            skLineSegment(sketch, "E71.top", {"start": v(-1516.68, 425) * mm, "end": v(-206.68, 425) * mm});
            skLineSegment(sketch, "E71.left", {"start": v(-1516.68, 430) * mm, "end": v(-1516.68, 425) * mm});
            skLineSegment(sketch, "E71.right", {"start": v(-206.68, 430) * mm, "end": v(-206.68, 425) * mm});
            skLineSegment(sketch, "E72.0.1.0", {"start": v(-1516.68, 330) * mm, "end": v(-206.68, 330) * mm});
            skLineSegment(sketch, "E72.0.1.1", {"start": v(-1516.68, 335) * mm, "end": v(-206.68, 335) * mm});
            skLineSegment(sketch, "E72.0.1.2", {"start": v(-1516.68, 335) * mm, "end": v(-1516.68, 330) * mm});
            skLineSegment(sketch, "E72.0.1.3", {"start": v(-206.68, 335) * mm, "end": v(-206.68, 330) * mm});
            skLineSegment(sketch, "E72.0.2.0", {"start": v(-1516.68, 235) * mm, "end": v(-206.68, 235) * mm});
            skLineSegment(sketch, "E72.0.2.1", {"start": v(-1516.68, 240) * mm, "end": v(-206.68, 240) * mm});
            skLineSegment(sketch, "E72.0.2.2", {"start": v(-1516.68, 240) * mm, "end": v(-1516.68, 235) * mm});
            skLineSegment(sketch, "E72.0.2.3", {"start": v(-206.68, 240) * mm, "end": v(-206.68, 235) * mm});
            skLineSegment(sketch, "E72.0.3.0", {"start": v(-1516.68, 140) * mm, "end": v(-206.68, 140) * mm});
            skLineSegment(sketch, "E72.0.3.1", {"start": v(-1516.68, 145) * mm, "end": v(-206.68, 145) * mm});
            skLineSegment(sketch, "E72.0.3.2", {"start": v(-1516.68, 145) * mm, "end": v(-1516.68, 140) * mm});
            skLineSegment(sketch, "E72.0.3.3", {"start": v(-206.68, 145) * mm, "end": v(-206.68, 140) * mm});
            skLineSegment(sketch, "E72.0.4.0", {"start": v(-1516.68, 45) * mm, "end": v(-206.68, 45) * mm});
            skLineSegment(sketch, "E72.0.4.1", {"start": v(-1516.68, 50) * mm, "end": v(-206.68, 50) * mm});
            skLineSegment(sketch, "E72.0.4.2", {"start": v(-1516.68, 50) * mm, "end": v(-1516.68, 45) * mm});
            skLineSegment(sketch, "E72.0.4.3", {"start": v(-206.68, 50) * mm, "end": v(-206.68, 45) * mm});
            skLineSegment(sketch, "E72.0.5.0", {"start": v(-1516.68, -50) * mm, "end": v(-206.68, -50) * mm});
            skLineSegment(sketch, "E72.0.5.1", {"start": v(-1516.68, -45) * mm, "end": v(-206.68, -45) * mm});
            skLineSegment(sketch, "E72.0.5.2", {"start": v(-1516.68, -45) * mm, "end": v(-1516.68, -50) * mm});
            skLineSegment(sketch, "E72.0.5.3", {"start": v(-206.68, -45) * mm, "end": v(-206.68, -50) * mm});
            skLineSegment(sketch, "E72.0.6.0", {"start": v(-1516.68, -145) * mm, "end": v(-206.68, -145) * mm});
            skLineSegment(sketch, "E72.0.6.1", {"start": v(-1516.68, -140) * mm, "end": v(-206.68, -140) * mm});
            skLineSegment(sketch, "E72.0.6.2", {"start": v(-1516.68, -140) * mm, "end": v(-1516.68, -145) * mm});
            skLineSegment(sketch, "E72.0.6.3", {"start": v(-206.68, -140) * mm, "end": v(-206.68, -145) * mm});
            skLineSegment(sketch, "E72.1.0.0", {"start": v(-1491.68, 425) * mm, "end": v(-181.68, 425) * mm});
            skLineSegment(sketch, "E72.1.0.1", {"start": v(-1491.68, 430) * mm, "end": v(-181.68, 430) * mm});
            skLineSegment(sketch, "E72.1.0.2", {"start": v(-1491.68, 430) * mm, "end": v(-1491.68, 425) * mm});
            skLineSegment(sketch, "E72.1.0.3", {"start": v(-181.68, 430) * mm, "end": v(-181.68, 425) * mm});
            skLineSegment(sketch, "E72.1.1.0", {"start": v(-1491.68, 330) * mm, "end": v(-181.68, 330) * mm});
            skLineSegment(sketch, "E72.1.1.1", {"start": v(-1491.68, 335) * mm, "end": v(-181.68, 335) * mm});
            skLineSegment(sketch, "E72.1.1.2", {"start": v(-1491.68, 335) * mm, "end": v(-1491.68, 330) * mm});
            skLineSegment(sketch, "E72.1.1.3", {"start": v(-181.68, 335) * mm, "end": v(-181.68, 330) * mm});
            skLineSegment(sketch, "E72.1.2.0", {"start": v(-1491.68, 235) * mm, "end": v(-181.68, 235) * mm});
            skLineSegment(sketch, "E72.1.2.1", {"start": v(-1491.68, 240) * mm, "end": v(-181.68, 240) * mm});
            skLineSegment(sketch, "E72.1.2.2", {"start": v(-1491.68, 240) * mm, "end": v(-1491.68, 235) * mm});
            skLineSegment(sketch, "E72.1.2.3", {"start": v(-181.68, 240) * mm, "end": v(-181.68, 235) * mm});
            skLineSegment(sketch, "E72.1.3.0", {"start": v(-1491.68, 140) * mm, "end": v(-181.68, 140) * mm});
            skLineSegment(sketch, "E72.1.3.1", {"start": v(-1491.68, 145) * mm, "end": v(-181.68, 145) * mm});
            skLineSegment(sketch, "E72.1.3.2", {"start": v(-1491.68, 145) * mm, "end": v(-1491.68, 140) * mm});
            skLineSegment(sketch, "E72.1.3.3", {"start": v(-181.68, 145) * mm, "end": v(-181.68, 140) * mm});
            skLineSegment(sketch, "E72.1.4.0", {"start": v(-1491.68, 45) * mm, "end": v(-181.68, 45) * mm});
            skLineSegment(sketch, "E72.1.4.1", {"start": v(-1491.68, 50) * mm, "end": v(-181.68, 50) * mm});
            skLineSegment(sketch, "E72.1.4.2", {"start": v(-1491.68, 50) * mm, "end": v(-1491.68, 45) * mm});
            skLineSegment(sketch, "E72.1.4.3", {"start": v(-181.68, 50) * mm, "end": v(-181.68, 45) * mm});
            skLineSegment(sketch, "E72.1.5.0", {"start": v(-1491.68, -50) * mm, "end": v(-181.68, -50) * mm});
            skLineSegment(sketch, "E72.1.5.1", {"start": v(-1491.68, -45) * mm, "end": v(-181.68, -45) * mm});
            skLineSegment(sketch, "E72.1.5.2", {"start": v(-1491.68, -45) * mm, "end": v(-1491.68, -50) * mm});
            skLineSegment(sketch, "E72.1.5.3", {"start": v(-181.68, -45) * mm, "end": v(-181.68, -50) * mm});
            skLineSegment(sketch, "E72.1.6.0", {"start": v(-1491.68, -145) * mm, "end": v(-181.68, -145) * mm});
            skLineSegment(sketch, "E72.1.6.1", {"start": v(-1491.68, -140) * mm, "end": v(-181.68, -140) * mm});
            skLineSegment(sketch, "E72.1.6.2", {"start": v(-1491.68, -140) * mm, "end": v(-1491.68, -145) * mm});
            skLineSegment(sketch, "E72.1.6.3", {"start": v(-181.68, -140) * mm, "end": v(-181.68, -145) * mm});
            skLineSegment(sketch, "E72.2.0.0", {"start": v(-1466.68, 425) * mm, "end": v(-156.68, 425) * mm});
            skLineSegment(sketch, "E72.2.0.1", {"start": v(-1466.68, 430) * mm, "end": v(-156.68, 430) * mm});
            skLineSegment(sketch, "E72.2.0.2", {"start": v(-1466.68, 430) * mm, "end": v(-1466.68, 425) * mm});
            skLineSegment(sketch, "E72.2.0.3", {"start": v(-156.68, 430) * mm, "end": v(-156.68, 425) * mm});
            skLineSegment(sketch, "E72.2.1.0", {"start": v(-1466.68, 330) * mm, "end": v(-156.68, 330) * mm});
            skLineSegment(sketch, "E72.2.1.1", {"start": v(-1466.68, 335) * mm, "end": v(-156.68, 335) * mm});
            skLineSegment(sketch, "E72.2.1.2", {"start": v(-1466.68, 335) * mm, "end": v(-1466.68, 330) * mm});
            skLineSegment(sketch, "E72.2.1.3", {"start": v(-156.68, 335) * mm, "end": v(-156.68, 330) * mm});
            skLineSegment(sketch, "E72.2.2.0", {"start": v(-1466.68, 235) * mm, "end": v(-156.68, 235) * mm});
            skLineSegment(sketch, "E72.2.2.1", {"start": v(-1466.68, 240) * mm, "end": v(-156.68, 240) * mm});
            skLineSegment(sketch, "E72.2.2.2", {"start": v(-1466.68, 240) * mm, "end": v(-1466.68, 235) * mm});
            skLineSegment(sketch, "E72.2.2.3", {"start": v(-156.68, 240) * mm, "end": v(-156.68, 235) * mm});
            skLineSegment(sketch, "E72.2.3.0", {"start": v(-1466.68, 140) * mm, "end": v(-156.68, 140) * mm});
            skLineSegment(sketch, "E72.2.3.1", {"start": v(-1466.68, 145) * mm, "end": v(-156.68, 145) * mm});
            skLineSegment(sketch, "E72.2.3.2", {"start": v(-1466.68, 145) * mm, "end": v(-1466.68, 140) * mm});
            skLineSegment(sketch, "E72.2.3.3", {"start": v(-156.68, 145) * mm, "end": v(-156.68, 140) * mm});
            skLineSegment(sketch, "E72.2.4.0", {"start": v(-1466.68, 45) * mm, "end": v(-156.68, 45) * mm});
            skLineSegment(sketch, "E72.2.4.1", {"start": v(-1466.68, 50) * mm, "end": v(-156.68, 50) * mm});
            skLineSegment(sketch, "E72.2.4.2", {"start": v(-1466.68, 50) * mm, "end": v(-1466.68, 45) * mm});
            skLineSegment(sketch, "E72.2.4.3", {"start": v(-156.68, 50) * mm, "end": v(-156.68, 45) * mm});
            skLineSegment(sketch, "E72.2.5.0", {"start": v(-1466.68, -50) * mm, "end": v(-156.68, -50) * mm});
            skLineSegment(sketch, "E72.2.5.1", {"start": v(-1466.68, -45) * mm, "end": v(-156.68, -45) * mm});
            skLineSegment(sketch, "E72.2.5.2", {"start": v(-1466.68, -45) * mm, "end": v(-1466.68, -50) * mm});
            skLineSegment(sketch, "E72.2.5.3", {"start": v(-156.68, -45) * mm, "end": v(-156.68, -50) * mm});
            skLineSegment(sketch, "E72.2.6.0", {"start": v(-1466.68, -145) * mm, "end": v(-156.68, -145) * mm});
            skLineSegment(sketch, "E72.2.6.1", {"start": v(-1466.68, -140) * mm, "end": v(-156.68, -140) * mm});
            skLineSegment(sketch, "E72.2.6.2", {"start": v(-1466.68, -140) * mm, "end": v(-1466.68, -145) * mm});
            skLineSegment(sketch, "E72.2.6.3", {"start": v(-156.68, -140) * mm, "end": v(-156.68, -145) * mm});
            skLineSegment(sketch, "E72.direction1", {"start": v(-1516.68, 425) * mm, "end": v(-1491.68, 425) * mm, "construction": true});
            skLineSegment(sketch, "E72.direction2", {"start": v(-1516.68, 425) * mm, "end": v(-1516.68, 330) * mm, "construction": true});
            skSolve(sketch);
        }
        {
            var Q0;
            {var subQ0=sQuery(id+"F33.wireOp",EDGE,"E71.right");Q0=makeQuery(id+"F33.imprint","IMPRINT",FACE,{"disambiguationData":[TD([[makeQuery(id+"F33.imprint","IMPRINT",EDGE,{"derivedFrom":subQ0}),-1.0]])]});}
            var Q1;
            {var subQ0=sQuery(id+"F33.wireOp",EDGE,"E72.0.1.3");Q1=makeQuery(id+"F33.imprint","IMPRINT",FACE,{"disambiguationData":[TD([[makeQuery(id+"F33.imprint","IMPRINT",EDGE,{"derivedFrom":subQ0}),-1.0]])]});}
            var Q2;
            {var subQ0=sQuery(id+"F33.wireOp",EDGE,"E72.0.2.3");Q2=makeQuery(id+"F33.imprint","IMPRINT",FACE,{"disambiguationData":[TD([[makeQuery(id+"F33.imprint","IMPRINT",EDGE,{"derivedFrom":subQ0}),-1.0]])]});}
            var Q3;
            {var subQ0=sQuery(id+"F33.wireOp",EDGE,"E72.0.3.3");Q3=makeQuery(id+"F33.imprint","IMPRINT",FACE,{"disambiguationData":[TD([[makeQuery(id+"F33.imprint","IMPRINT",EDGE,{"derivedFrom":subQ0}),-1.0]])]});}
            var Q4;
            {var subQ0=sQuery(id+"F33.wireOp",EDGE,"E72.0.4.3");Q4=makeQuery(id+"F33.imprint","IMPRINT",FACE,{"disambiguationData":[TD([[makeQuery(id+"F33.imprint","IMPRINT",EDGE,{"derivedFrom":subQ0}),-1.0]])]});}
            extrude(context, id + "F34", {"entities" : qUnion([Q0, Q1, Q2, Q3, Q4]), "operationType" : NewBodyOperationType.REMOVE, "oppositeDirection" : true, "depth" : 444 * mm, "offsetDistance" : 25 * mm});
        }
        {
            var Q0;
            Q0=makeQuery(id+"F32.opExtrude","CAP_FACE",FACE,{"disambiguationData":[OSD([sQuery(id+"F31.wireOp",EDGE,"E70.bottom"),sQuery(id+"F31.wireOp",EDGE,"E70.top"),sQuery(id+"F31.wireOp",EDGE,"E70.left"),sQuery(id+"F31.wireOp",EDGE,"E70.right")])],"isStart":false});
            var sketch = newSketch(context, id + "F35", { "sketchPlane" : qUnion([Q0])});
            skLineSegment(sketch, "E73.0", {"start": v(-10240.47, 181.68) * mm, "end": v(-9980.47, 181.68) * mm});
            skLineSegment(sketch, "E73.1", {"start": v(-10240.47, 1541.68) * mm, "end": v(-10240.47, 181.68) * mm});
            skLineSegment(sketch, "E73.2", {"start": v(-9980.47, 1541.68) * mm, "end": v(-10240.47, 1541.68) * mm});
            skLineSegment(sketch, "E73.3", {"start": v(-9980.47, 181.68) * mm, "end": v(-9980.47, 1541.68) * mm});
            skSolve(sketch);
        }
        {
            var Q0;
            Q0=makeQuery(id+"F35.imprint","IMPRINT",FACE,{"disambiguationData":[TD([[makeQuery(id+"F35.imprint","IMPRINT",EDGE,{"derivedFrom":sQuery(id+"F35.wireOp",EDGE,"E73.0")}),1.0]])]});
            extrude(context, id + "F36", {"entities" : qUnion([Q0]), "operationType" : NewBodyOperationType.REMOVE, "oppositeDirection" : true, "depth" : 444 * mm, "offsetDistance" : 25 * mm});
        }
        {
            var Q0;
            Q0=makeQuery(id+"F32.opExtrude","CAP_FACE",FACE,{"disambiguationData":[OSD([sQuery(id+"F31.wireOp",EDGE,"E70.bottom"),sQuery(id+"F31.wireOp",EDGE,"E70.top"),sQuery(id+"F31.wireOp",EDGE,"E70.left"),sQuery(id+"F31.wireOp",EDGE,"E70.right")])],"isStart":false});
            var sketch = newSketch(context, id + "F37", { "sketchPlane" : qUnion([Q0])});
            skLineSegment(sketch, "E74.bottom", {"start": v(-10310.47, 111.68) * mm, "end": v(-10240.47, 111.68) * mm});
            skLineSegment(sketch, "E74.top", {"start": v(-10310.47, 181.68) * mm, "end": v(-10240.47, 181.68) * mm});
            skLineSegment(sketch, "E74.left", {"start": v(-10310.47, 111.68) * mm, "end": v(-10310.47, 181.68) * mm});
            skLineSegment(sketch, "E74.right", {"start": v(-10240.47, 111.68) * mm, "end": v(-10240.47, 181.68) * mm});
            skLineSegment(sketch, "E75.bottom", {"start": v(-10310.47, 1611.68) * mm, "end": v(-10240.47, 1611.68) * mm});
            skLineSegment(sketch, "E75.top", {"start": v(-10310.47, 1541.68) * mm, "end": v(-10240.47, 1541.68) * mm});
            skLineSegment(sketch, "E75.left", {"start": v(-10310.47, 1611.68) * mm, "end": v(-10310.47, 1541.68) * mm});
            skLineSegment(sketch, "E75.right", {"start": v(-10240.47, 1611.68) * mm, "end": v(-10240.47, 1541.68) * mm});
            skSolve(sketch);
        }
        {
            var Q0;
            Q0=makeQuery(id+"F37.imprint","IMPRINT",FACE,{"disambiguationData":[TD([[makeQuery(id+"F37.imprint","IMPRINT",EDGE,{"derivedFrom":sQuery(id+"F37.wireOp",EDGE,"E74.bottom")}),-1.0]])]});
            var Q1;
            Q1=makeQuery(id+"F37.imprint","IMPRINT",FACE,{"disambiguationData":[TD([[makeQuery(id+"F37.imprint","IMPRINT",EDGE,{"derivedFrom":sQuery(id+"F37.wireOp",EDGE,"E75.bottom")}),1.0]])]});
            extrude(context, id + "F38", {"entities" : qUnion([Q0, Q1]), "operationType" : NewBodyOperationType.ADD, "depth" : 1200 * mm, "offsetDistance" : 25 * mm});
        }
        {
            var Q0;
            Q0=makeQuery(id+"F38.opExtrude","SWEPT_FACE",FACE,{"disambiguationData":[OSD([sQuery(id+"F37.wireOp",EDGE,"E74.right")])]});
            var sketch = newSketch(context, id + "F39", { "sketchPlane" : qUnion([Q0])});
            skLineSegment(sketch, "E76.bottom", {"start": v(115.8, 1891.36) * mm, "end": v(1475.8, 1891.36) * mm});
            skLineSegment(sketch, "E76.top", {"start": v(115.8, 1896.36) * mm, "end": v(1475.8, 1896.36) * mm});
            skLineSegment(sketch, "E76.left", {"start": v(115.8, 1891.36) * mm, "end": v(115.8, 1896.36) * mm});
            skLineSegment(sketch, "E76.right", {"start": v(1475.8, 1891.36) * mm, "end": v(1475.8, 1896.36) * mm});
            skSolve(sketch);
        }
        {
            var Q0;
            Q0=makeQuery(id+"F39.imprint","IMPRINT",FACE,{"disambiguationData":[TD([[makeQuery(id+"F39.imprint","IMPRINT",EDGE,{"derivedFrom":sQuery(id+"F39.wireOp",EDGE,"E76.bottom")}),1.0]])]});
            extrude(context, id + "F40", {"entities" : qUnion([Q0]), "depth" : 5 * mm, "offsetDistance" : 25 * mm});
        }
        {
            var Q0;
            Q0=makeQuery(id+"F38.boolean.opBoolean","MERGE",FACE,{"derivedFrom":[makeQuery(id+"F32.opExtrude","SWEPT_FACE",FACE,{"disambiguationData":[OSD([sQuery(id+"F31.wireOp",EDGE,"E70.top")])]}),makeQuery(id+"F38.opExtrude","SWEPT_FACE",FACE,{"disambiguationData":[OSD([sQuery(id+"F37.wireOp",EDGE,"E74.bottom")])]})]});
            var sketch = newSketch(context, id + "F41", { "sketchPlane" : qUnion([Q0])});
            skLineSegment(sketch, "E77.bottom", {"start": v(-11642.16, 1728.85) * mm, "end": v(-11337.16, 1728.85) * mm});
            skLineSegment(sketch, "E77.top", {"start": v(-11642.16, 528.85) * mm, "end": v(-11337.16, 528.85) * mm});
            skLineSegment(sketch, "E77.left", {"start": v(-11642.16, 1728.85) * mm, "end": v(-11642.16, 528.85) * mm});
            skLineSegment(sketch, "E77.right", {"start": v(-11337.16, 1728.85) * mm, "end": v(-11337.16, 528.85) * mm});
            skLineSegment(sketch, "E78.bottom", {"start": v(-11584.66, 1723.85) * mm, "end": v(-11394.66, 1723.85) * mm});
            skLineSegment(sketch, "E78.left", {"start": v(-11584.66, 1723.85) * mm, "end": v(-11584.66, 1528.85) * mm});
            skLineSegment(sketch, "E78.right", {"start": v(-11394.66, 1723.85) * mm, "end": v(-11394.66, 1528.85) * mm});
            skLineSegment(sketch, "E79", {"start": v(-11389.66, 1723.85) * mm, "end": v(-11337.16, 1723.85) * mm});
            skLineSegment(sketch, "E80", {"start": v(-11589.66, 1723.85) * mm, "end": v(-11642.16, 1723.85) * mm});
            skLineSegment(sketch, "E81", {"start": v(-11389.66, 1723.85) * mm, "end": v(-11389.66, 1528.85) * mm});
            skLineSegment(sketch, "E82", {"start": v(-11389.66, 1528.85) * mm, "end": v(-11394.66, 1528.85) * mm});
            skLineSegment(sketch, "E83", {"start": v(-11589.66, 1723.85) * mm, "end": v(-11589.66, 1528.85) * mm});
            skLineSegment(sketch, "E84", {"start": v(-11589.66, 1528.85) * mm, "end": v(-11584.66, 1528.85) * mm});
            skLineSegment(sketch, "E85.0.1.0", {"start": v(-11389.66, 1523.85) * mm, "end": v(-11337.16, 1523.85) * mm});
            skLineSegment(sketch, "E85.0.1.1", {"start": v(-11394.66, 1523.85) * mm, "end": v(-11394.66, 1328.85) * mm});
            skLineSegment(sketch, "E85.0.1.2", {"start": v(-11589.66, 1523.85) * mm, "end": v(-11589.66, 1328.85) * mm});
            skLineSegment(sketch, "E85.0.1.3", {"start": v(-11389.66, 1523.85) * mm, "end": v(-11389.66, 1328.85) * mm});
            skLineSegment(sketch, "E85.0.1.4", {"start": v(-11584.66, 1523.85) * mm, "end": v(-11584.66, 1328.85) * mm});
            skLineSegment(sketch, "E85.0.1.5", {"start": v(-11642.16, 1528.85) * mm, "end": v(-11337.16, 1528.85) * mm});
            skLineSegment(sketch, "E85.0.1.6", {"start": v(-11584.66, 1523.85) * mm, "end": v(-11394.66, 1523.85) * mm});
            skLineSegment(sketch, "E85.0.1.7", {"start": v(-11589.66, 1523.85) * mm, "end": v(-11642.16, 1523.85) * mm});
            skLineSegment(sketch, "E85.0.1.8", {"start": v(-11589.66, 1328.85) * mm, "end": v(-11584.66, 1328.85) * mm});
            skLineSegment(sketch, "E85.0.1.9", {"start": v(-11389.66, 1328.85) * mm, "end": v(-11394.66, 1328.85) * mm});
            skLineSegment(sketch, "E85.0.2.0", {"start": v(-11389.66, 1323.85) * mm, "end": v(-11337.16, 1323.85) * mm});
            skLineSegment(sketch, "E85.0.2.1", {"start": v(-11394.66, 1323.85) * mm, "end": v(-11394.66, 1128.85) * mm});
            skLineSegment(sketch, "E85.0.2.2", {"start": v(-11589.66, 1323.85) * mm, "end": v(-11589.66, 1128.85) * mm});
            skLineSegment(sketch, "E85.0.2.3", {"start": v(-11389.66, 1323.85) * mm, "end": v(-11389.66, 1128.85) * mm});
            skLineSegment(sketch, "E85.0.2.4", {"start": v(-11584.66, 1323.85) * mm, "end": v(-11584.66, 1128.85) * mm});
            skLineSegment(sketch, "E85.0.2.5", {"start": v(-11642.16, 1328.85) * mm, "end": v(-11337.16, 1328.85) * mm});
            skLineSegment(sketch, "E85.0.2.6", {"start": v(-11584.66, 1323.85) * mm, "end": v(-11394.66, 1323.85) * mm});
            skLineSegment(sketch, "E85.0.2.7", {"start": v(-11589.66, 1323.85) * mm, "end": v(-11642.16, 1323.85) * mm});
            skLineSegment(sketch, "E85.0.2.8", {"start": v(-11589.66, 1128.85) * mm, "end": v(-11584.66, 1128.85) * mm});
            skLineSegment(sketch, "E85.0.2.9", {"start": v(-11389.66, 1128.85) * mm, "end": v(-11394.66, 1128.85) * mm});
            skLineSegment(sketch, "E85.0.3.0", {"start": v(-11389.66, 1123.85) * mm, "end": v(-11337.16, 1123.85) * mm});
            skLineSegment(sketch, "E85.0.3.1", {"start": v(-11394.66, 1123.85) * mm, "end": v(-11394.66, 928.85) * mm});
            skLineSegment(sketch, "E85.0.3.2", {"start": v(-11589.66, 1123.85) * mm, "end": v(-11589.66, 928.85) * mm});
            skLineSegment(sketch, "E85.0.3.3", {"start": v(-11389.66, 1123.85) * mm, "end": v(-11389.66, 928.85) * mm});
            skLineSegment(sketch, "E85.0.3.4", {"start": v(-11584.66, 1123.85) * mm, "end": v(-11584.66, 928.85) * mm});
            skLineSegment(sketch, "E85.0.3.5", {"start": v(-11642.16, 1128.85) * mm, "end": v(-11337.16, 1128.85) * mm});
            skLineSegment(sketch, "E85.0.3.6", {"start": v(-11584.66, 1123.85) * mm, "end": v(-11394.66, 1123.85) * mm});
            skLineSegment(sketch, "E85.0.3.7", {"start": v(-11589.66, 1123.85) * mm, "end": v(-11642.16, 1123.85) * mm});
            skLineSegment(sketch, "E85.0.3.8", {"start": v(-11589.66, 928.85) * mm, "end": v(-11584.66, 928.85) * mm});
            skLineSegment(sketch, "E85.0.3.9", {"start": v(-11389.66, 928.85) * mm, "end": v(-11394.66, 928.85) * mm});
            skLineSegment(sketch, "E85.0.4.0", {"start": v(-11389.66, 923.85) * mm, "end": v(-11337.16, 923.85) * mm});
            skLineSegment(sketch, "E85.0.4.1", {"start": v(-11394.66, 923.85) * mm, "end": v(-11394.66, 728.85) * mm});
            skLineSegment(sketch, "E85.0.4.2", {"start": v(-11589.66, 923.85) * mm, "end": v(-11589.66, 728.85) * mm});
            skLineSegment(sketch, "E85.0.4.3", {"start": v(-11389.66, 923.85) * mm, "end": v(-11389.66, 728.85) * mm});
            skLineSegment(sketch, "E85.0.4.4", {"start": v(-11584.66, 923.85) * mm, "end": v(-11584.66, 728.85) * mm});
            skLineSegment(sketch, "E85.0.4.5", {"start": v(-11642.16, 928.85) * mm, "end": v(-11337.16, 928.85) * mm});
            skLineSegment(sketch, "E85.0.4.6", {"start": v(-11584.66, 923.85) * mm, "end": v(-11394.66, 923.85) * mm});
            skLineSegment(sketch, "E85.0.4.7", {"start": v(-11589.66, 923.85) * mm, "end": v(-11642.16, 923.85) * mm});
            skLineSegment(sketch, "E85.0.4.8", {"start": v(-11589.66, 728.85) * mm, "end": v(-11584.66, 728.85) * mm});
            skLineSegment(sketch, "E85.0.4.9", {"start": v(-11389.66, 728.85) * mm, "end": v(-11394.66, 728.85) * mm});
            skLineSegment(sketch, "E85.0.5.0", {"start": v(-11389.66, 723.85) * mm, "end": v(-11337.16, 723.85) * mm});
            skLineSegment(sketch, "E85.0.5.1", {"start": v(-11394.66, 723.85) * mm, "end": v(-11394.66, 528.85) * mm});
            skLineSegment(sketch, "E85.0.5.2", {"start": v(-11589.66, 723.85) * mm, "end": v(-11589.66, 528.85) * mm});
            skLineSegment(sketch, "E85.0.5.3", {"start": v(-11389.66, 723.85) * mm, "end": v(-11389.66, 528.85) * mm});
            skLineSegment(sketch, "E85.0.5.4", {"start": v(-11584.66, 723.85) * mm, "end": v(-11584.66, 528.85) * mm});
            skLineSegment(sketch, "E85.0.5.5", {"start": v(-11642.16, 728.85) * mm, "end": v(-11337.16, 728.85) * mm});
            skLineSegment(sketch, "E85.0.5.6", {"start": v(-11584.66, 723.85) * mm, "end": v(-11394.66, 723.85) * mm});
            skLineSegment(sketch, "E85.0.5.7", {"start": v(-11589.66, 723.85) * mm, "end": v(-11642.16, 723.85) * mm});
            skLineSegment(sketch, "E85.0.5.8", {"start": v(-11589.66, 528.85) * mm, "end": v(-11584.66, 528.85) * mm});
            skLineSegment(sketch, "E85.0.5.9", {"start": v(-11389.66, 528.85) * mm, "end": v(-11394.66, 528.85) * mm});
            skLineSegment(sketch, "E85.direction1", {"start": v(-11589.66, 1528.85) * mm, "end": v(-11564.66, 1528.85) * mm, "construction": true});
            skLineSegment(sketch, "E85.direction2", {"start": v(-11589.66, 1528.85) * mm, "end": v(-11589.66, 1328.85) * mm, "construction": true});
            skSolve(sketch);
        }
        {
            var Q0;
            Q0=makeQuery(id+"F41.imprint","IMPRINT",FACE,{"disambiguationData":[TD([[makeQuery(id+"F41.imprint","IMPRINT",EDGE,{"derivedFrom":sQuery(id+"F41.wireOp",EDGE,"E77.bottom")}),-1.0]])]});
            var Q1;
            {var subQ4=sQuery(id+"F41.wireOp",EDGE,"E85.0.1.0");Q1=makeQuery(id+"F41.imprint","IMPRINT",FACE,{"disambiguationData":[TD([[makeQuery(id+"F41.imprint","IMPRINT",EDGE,{"derivedFrom":subQ4}),1.0]])]});}
            var Q2;
            {var subQ11=sQuery(id+"F41.wireOp",EDGE,"E85.0.2.0");Q2=makeQuery(id+"F41.imprint","IMPRINT",FACE,{"disambiguationData":[TD([[makeQuery(id+"F41.imprint","IMPRINT",EDGE,{"derivedFrom":subQ11}),1.0]])]});}
            var Q3;
            {var subQ12=sQuery(id+"F41.wireOp",EDGE,"E85.0.3.0");Q3=makeQuery(id+"F41.imprint","IMPRINT",FACE,{"disambiguationData":[TD([[makeQuery(id+"F41.imprint","IMPRINT",EDGE,{"derivedFrom":subQ12}),1.0]])]});}
            var Q4;
            {var subQ11=sQuery(id+"F41.wireOp",EDGE,"E85.0.4.0");Q4=makeQuery(id+"F41.imprint","IMPRINT",FACE,{"disambiguationData":[TD([[makeQuery(id+"F41.imprint","IMPRINT",EDGE,{"derivedFrom":subQ11}),1.0]])]});}
            var Q5;
            {var subQ7=sQuery(id+"F41.wireOp",EDGE,"E85.0.5.0");Q5=makeQuery(id+"F41.imprint","IMPRINT",FACE,{"disambiguationData":[TD([[makeQuery(id+"F41.imprint","IMPRINT",EDGE,{"derivedFrom":subQ7}),1.0]])]});}
            extrude(context, id + "F42", {"entities" : qUnion([Q0, Q1, Q2, Q3, Q4, Q5]), "depth" : 5 * mm, "offsetDistance" : 25 * mm});
        }
        {
            var Q0;
            Q0=makeQuery(id+"F38.opExtrude","SWEPT_FACE",FACE,{"disambiguationData":[OSD([sQuery(id+"F37.wireOp",EDGE,"E74.right")])]});
            var sketch = newSketch(context, id + "F43", { "sketchPlane" : qUnion([Q0])});
            skLineSegment(sketch, "E86.bottom", {"start": v(1796.07, 2136.57) * mm, "end": v(296.07, 2136.57) * mm});
            skLineSegment(sketch, "E86.top", {"start": v(1796.07, 2181.57) * mm, "end": v(296.07, 2181.57) * mm});
            skLineSegment(sketch, "E86.left", {"start": v(1796.07, 2136.57) * mm, "end": v(1796.07, 2181.57) * mm});
            skLineSegment(sketch, "E86.right", {"start": v(296.07, 2136.57) * mm, "end": v(296.07, 2181.57) * mm});
            skSolve(sketch);
        }
        {
            var Q0;
            Q0=makeQuery(id+"F43.imprint","IMPRINT",FACE,{"disambiguationData":[TD([[makeQuery(id+"F43.imprint","IMPRINT",EDGE,{"derivedFrom":sQuery(id+"F43.wireOp",EDGE,"E86.bottom")}),-1.0]])]});
            extrude(context, id + "F44", {"entities" : qUnion([Q0]), "depth" : 45 * mm, "offsetDistance" : 25 * mm});
        }
        {
            var Q0;
            {var subQ0=sQuery(id+"F11.wireOp",EDGE,"E20.top");var subQ1=sQuery(id+"F11.wireOp",EDGE,"E20.bottom");var subQ2=sQuery(id+"F11.wireOp",EDGE,"E20.right");var subQ3=makeQuery(id+"F12.opExtrude","CAP_FACE",FACE,{"disambiguationData":[OSD([subQ1,subQ0,sQuery(id+"F11.wireOp",EDGE,"E20.left"),subQ2])],"isStart":false});Q0=makeQuery(id+"F20.boolean.opBoolean","SPLIT",FACE,{"disambiguationData":[TD([makeQuery(id+"F12.opExtrude","SWEPT_FACE",FACE,{"disambiguationData":[OSD([subQ1])]})])],"derivedFrom":subQ3});}
            var sketch = newSketch(context, id + "F45", { "sketchPlane" : qUnion([Q0])});
            skLineSegment(sketch, "E87.bottom", {"start": v(-8690.89, 2709.16) * mm, "end": v(-8810.89, 2709.16) * mm});
            skLineSegment(sketch, "E87.top", {"start": v(-8690.89, -2090.84) * mm, "end": v(-8810.89, -2090.84) * mm});
            skLineSegment(sketch, "E87.left", {"start": v(-8690.89, 2709.16) * mm, "end": v(-8690.89, -2090.84) * mm});
            skLineSegment(sketch, "E87.right", {"start": v(-8810.89, 2709.16) * mm, "end": v(-8810.89, -2090.84) * mm});
            skSolve(sketch);
        }
        {
            var Q0;
            Q0=makeQuery(id+"F45.imprint","IMPRINT",FACE,{"disambiguationData":[TD([[makeQuery(id+"F45.imprint","IMPRINT",EDGE,{"derivedFrom":sQuery(id+"F45.wireOp",EDGE,"E87.bottom")}),1.0]])]});
            extrude(context, id + "F46", {"entities" : qUnion([Q0]), "depth" : 28 * mm, "offsetDistance" : 25 * mm});
        }
        {
            var Q0;
            {var subQ0=sQuery(id+"F11.wireOp",EDGE,"E20.top");var subQ1=sQuery(id+"F11.wireOp",EDGE,"E20.bottom");var subQ2=sQuery(id+"F11.wireOp",EDGE,"E20.right");var subQ3=makeQuery(id+"F12.opExtrude","CAP_FACE",FACE,{"disambiguationData":[OSD([subQ1,subQ0,sQuery(id+"F11.wireOp",EDGE,"E20.left"),subQ2])],"isStart":false});Q0=makeQuery(id+"F20.boolean.opBoolean","SPLIT",FACE,{"disambiguationData":[TD([makeQuery(id+"F12.opExtrude","SWEPT_FACE",FACE,{"disambiguationData":[OSD([subQ1])]})])],"derivedFrom":subQ3});}
            var sketch = newSketch(context, id + "F47", { "sketchPlane" : qUnion([Q0])});
            skLineSegment(sketch, "E88.bottom", {"start": v(-8380.01, 1387.53) * mm, "end": v(-8310.01, 1387.53) * mm});
            skLineSegment(sketch, "E88.top", {"start": v(-8380.01, 1317.53) * mm, "end": v(-8310.01, 1317.53) * mm});
            skLineSegment(sketch, "E88.left", {"start": v(-8380.01, 1387.53) * mm, "end": v(-8380.01, 1317.53) * mm});
            skLineSegment(sketch, "E88.right", {"start": v(-8310.01, 1387.53) * mm, "end": v(-8310.01, 1317.53) * mm});
            skSolve(sketch);
        }
        {
            var Q0;
            Q0=makeQuery(id+"F47.imprint","IMPRINT",FACE,{"disambiguationData":[TD([[makeQuery(id+"F47.imprint","IMPRINT",EDGE,{"derivedFrom":sQuery(id+"F47.wireOp",EDGE,"E88.bottom")}),-1.0]])]});
            extrude(context, id + "F48", {"entities" : qUnion([Q0]), "depth" : 422 * mm, "offsetDistance" : 25 * mm});
        }
        {
            var Q0;
            Q0=makeQuery(id+"F44.opExtrude","CAP_FACE",FACE,{"disambiguationData":[OSD([sQuery(id+"F43.wireOp",EDGE,"E86.bottom"),sQuery(id+"F43.wireOp",EDGE,"E86.top"),sQuery(id+"F43.wireOp",EDGE,"E86.left"),sQuery(id+"F43.wireOp",EDGE,"E86.right")])],"isStart":false});
            var sketch = newSketch(context, id + "F49", { "sketchPlane" : qUnion([Q0])});
            skLineSegment(sketch, "E89.bottom", {"start": v(-2061.28, 2472.8) * mm, "end": v(3938.72, 2472.8) * mm});
            skLineSegment(sketch, "E89.top", {"start": v(-2061.28, 2427.8) * mm, "end": v(3938.72, 2427.8) * mm});
            skLineSegment(sketch, "E89.left", {"start": v(-2061.28, 2472.8) * mm, "end": v(-2061.28, 2427.8) * mm});
            skLineSegment(sketch, "E89.right", {"start": v(3938.72, 2472.8) * mm, "end": v(3938.72, 2427.8) * mm});
            skSolve(sketch);
        }
        {
            var Q0;
            Q0=makeQuery(id+"F49.imprint","IMPRINT",FACE,{"disambiguationData":[TD([[makeQuery(id+"F49.imprint","IMPRINT",EDGE,{"derivedFrom":sQuery(id+"F49.wireOp",EDGE,"E89.bottom")}),-1.0]])]});
            extrude(context, id + "F50", {"entities" : qUnion([Q0]), "depth" : 45 * mm, "offsetDistance" : 25 * mm});
        }
    });
